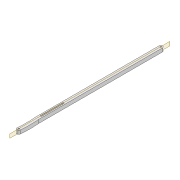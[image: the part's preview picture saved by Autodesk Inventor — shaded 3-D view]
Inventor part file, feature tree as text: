
AUTODESK INVENTOR PART (.ipt)
format: ipt  version: 2022 (Build 260153000, 153)  size: 105,472 bytes
history: native  units: mm
features: extrude x1, sketch x1
ambient origin geometry x8: Origin, YZ Plane, XZ Plane, XY Plane, X Axis, Y Axis, Z Axis, Center Point
bodies: Solid1 (feature_tree)
feature tree (2):
  extrude  "Extrusion1"  Depth=8.0mm
  sketch  "Sketch1"  dims[d0=319.927mm d1=8.0mm d2=3.0mm d3=3.0mm d4=8.0mm d5=0.0mm d12=3.0mm d13=50.8mm d14=100.0mm d15=40.0mm d16=200.0mm d17=200.0mm]
